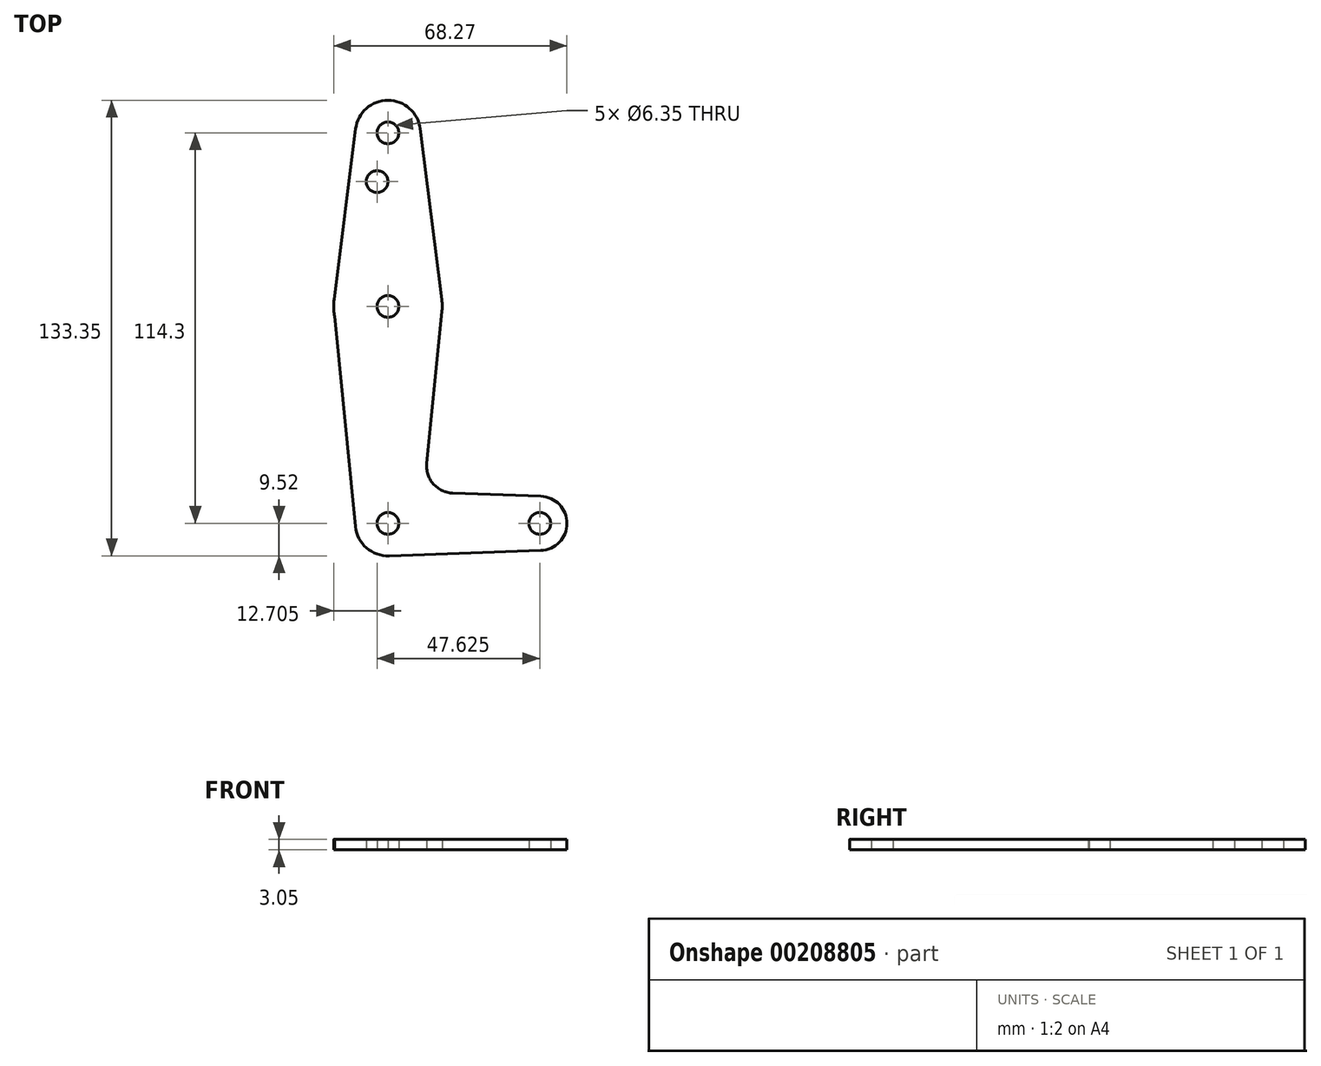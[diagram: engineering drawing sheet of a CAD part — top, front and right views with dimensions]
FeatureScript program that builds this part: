
annotation { "Feature Type Name" : "Feature", "Feature Type Description" : "" }
export const myFeature = defineFeature(function(context is Context, id is Id, definition is map)
    precondition{}
    {
        {
            var Q0;
            Q0=qCreatedBy(makeId("Top.planeOp"),FACE);
            var sketch = newSketch(context, id + "F0", { "sketchPlane" : qUnion([Q0])});
            skLineSegment(sketch, "E0", {"start": v(0, 0) * mm, "end": v(0, 114.3) * mm, "construction": true});
            skLineSegment(sketch, "E1", {"start": v(0, 0) * mm, "end": v(44.45, 0) * mm, "construction": true});
            skCircle(sketch, "E2", {"center": v(0, 114.3) * mm, "radius": 9.53 * mm});
            skCircle(sketch, "E3", {"center": v(0, 63.5) * mm, "radius": 15.88 * mm});
            skCircle(sketch, "E4", {"center": v(44.45, 0) * mm, "radius": 7.94 * mm});
            skCircle(sketch, "E5", {"center": v(0, 0) * mm, "radius": 9.53 * mm});
            skLineSegment(sketch, "E6", {"start": v(-9.45, 115.5) * mm, "end": v(-15.75, 65.48) * mm});
            skLineSegment(sketch, "E7", {"start": v(9.45, 115.5) * mm, "end": v(15.75, 65.48) * mm});
            skCircle(sketch, "E8", {"center": v(0, 114.3) * mm, "radius": 3.18 * mm});
            skCircle(sketch, "E9", {"center": v(-3.18, 100.03) * mm, "radius": 3.18 * mm});
            skCircle(sketch, "E10", {"center": v(0, 0) * mm, "radius": 3.18 * mm});
            skCircle(sketch, "E11", {"center": v(44.45, 0) * mm, "radius": 3.18 * mm});
            skCircle(sketch, "E12", {"center": v(0, 63.5) * mm, "radius": 3.18 * mm});
            skLineSegment(sketch, "E13", {"start": v(-15.62, 60.67) * mm, "end": v(-9.48, -0.94) * mm});
            skLineSegment(sketch, "E14", {"start": v(15.8, 61.91) * mm, "end": v(11.34, 17.6) * mm});
            skLineSegment(sketch, "E15", {"start": v(18.97, 8.85) * mm, "end": v(44.73, 7.93) * mm});
            skLineSegment(sketch, "E16", {"start": v(0.34, -9.52) * mm, "end": v(44.73, -7.93) * mm});
            skArc(sketch, "E17.filletArc", {"start": v(11.34, 17.6) * mm, "mid": v(13.26, 11.57) * mm, "end": v(18.97, 8.85) * mm});
            skSolve(sketch);
        }
        {
            var Q0;
            Q0 = qSketchRegion(id + "F0", true);
            extrude(context, id + "F1", {"entities" : qUnion([Q0]), "depth" : 3.05 * mm});
        }
    });
